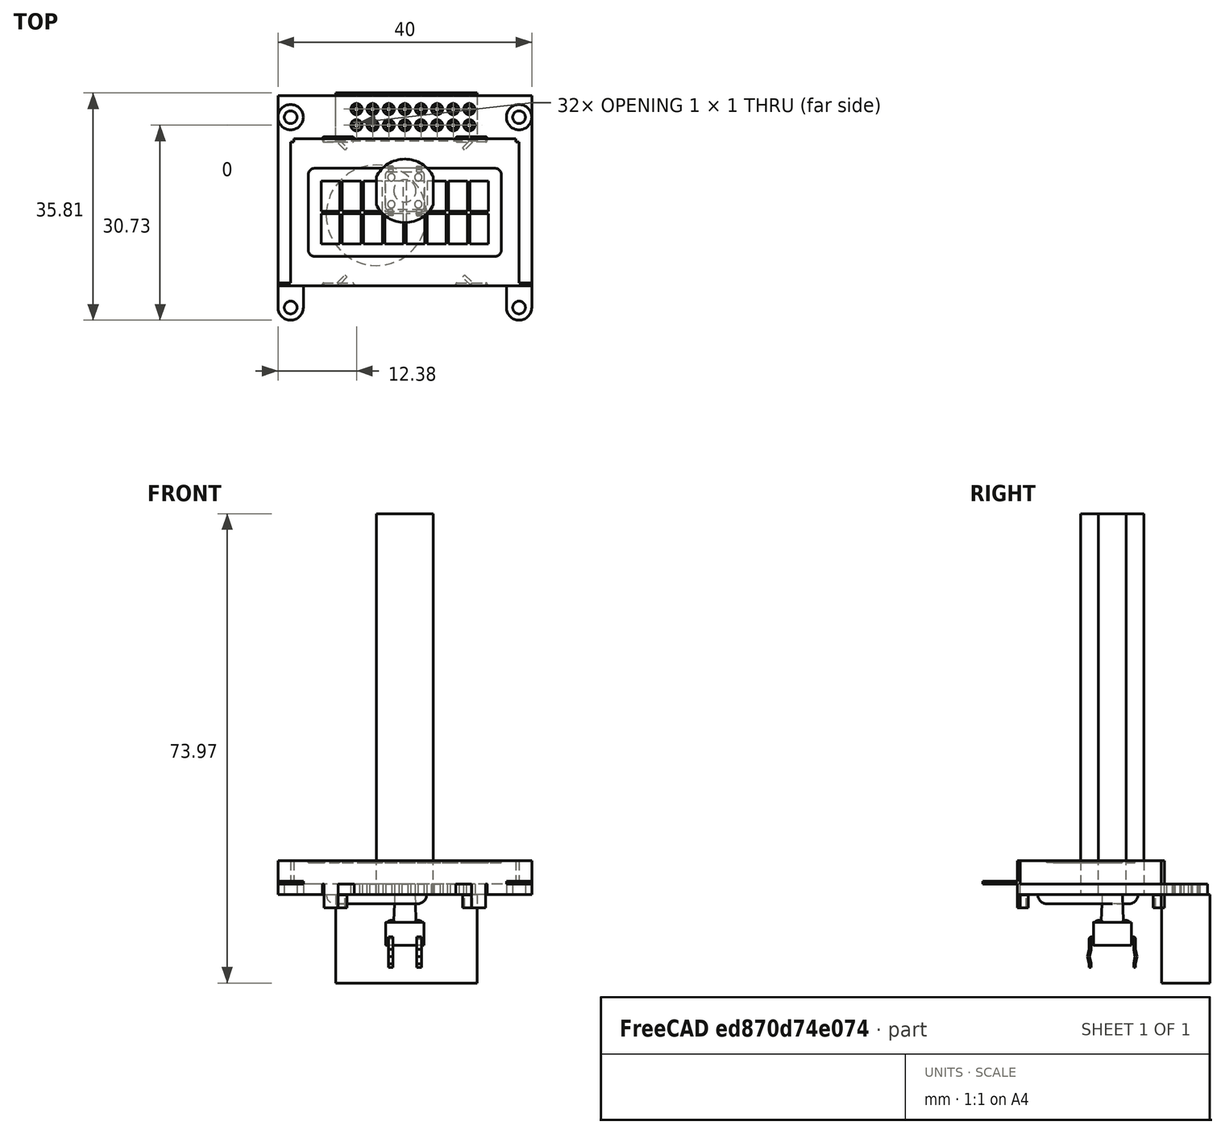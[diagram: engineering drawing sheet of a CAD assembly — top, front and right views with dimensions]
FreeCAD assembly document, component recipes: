
FREECAD ASSEMBLY — COMPONENT RECIPES ("WwvbClockComponents")

This assembly document has 6 components, labeled P0..P5 below (a component is one placed body or linked part). 4 of them carry a construction recipe — the FreeCAD feature program that regenerates the part from scratch, quoted from this document or its linked companion documents; the rest are supplied as boundary geometry only. No exploded tour is included for this assembly.
COMPONENT P0 — recipe-attached ("LCD panel001", modeled in this document).
Construction recipe (the document's own serialized feature program — sketch geometry with constraints, then the solid features built on it; lengths are millimeters unless a unit is written):

FEATURE [PartDesign::SubShapeBinder] Binder001
  BindCopyOnChange = 0
  BindMode = 0
  ClaimChildren = false
  Context = -> NHD_0208AZ_RN [Body.Binder001.]
  Fuse = false
  MakeFace = true
  OffsetFill = false
  OffsetIntersection = false
  OffsetJoinType = 0
  OffsetOpenResult = false
  PartialLoad = false
  Refine = true
  Relative = true
  Support = -> [Part__Feature018]
  _Version = 2
FEATURE [Sketcher::SketchObject] Sketch
  ArcFitTolerance = 1e-06
  AttachmentSupport = -> [Binder001]
  ExternalGeometry = -> [Binder001]
  FullyConstrained = true
  MakeInternals = false
  MapMode = 5
  Placement = pos=(0,0,0) rot=(1,0,0;3.14159rad)
  sketch-geometry (4):
    g0: LineSegment StartX=-10.922 StartY=-7.79 StartZ=0 EndX=-10.922 EndY=-15.41 EndZ=0
    g1: LineSegment StartX=-10.922 StartY=-15.41 StartZ=0 EndX=11.422 EndY=-15.41 EndZ=0
    g2: LineSegment StartX=11.422 StartY=-15.41 StartZ=0 EndX=11.422 EndY=-7.79 EndZ=0
    g3: LineSegment StartX=11.422 StartY=-7.79 StartZ=0 EndX=-10.922 EndY=-7.79 EndZ=0
  constraints (12):
    c: Coincident(g0,g1)
    c: Coincident(g1,g2)
    c: Coincident(g2,g3)
    c: Coincident(g3,g0)
    c: Vertical(g0)
    c: Vertical(g2)
    c: Horizontal(g1)
    c: Horizontal(g3)
    c: DistanceX(g0,g-4) = 3.302
    c: DistanceX(g-3,g2) = 3.302
    c: DistanceY(g0,g-4) = 2.54
    c: DistanceY(g-3,g2) = 2.54
FEATURE [PartDesign::Pad] Pad
  Direction = (0,0,-1)
  Length = 13.97
  Length2 = 10
  Profile = -> Sketch
  ReferenceAxis = -> Sketch [N_Axis]
  Refine = true
  Suppressed = false
  Type = 0
FEATURE [PartDesign::Body] Body
  AllowCompound = false
  Group = -> [Binder001,Sketch,Pad]
  Origin = -> Origin019
  Tip = -> Pad
COMPONENT P1 — recipe-attached ("LED", a linked part whose construction recipe lives in a companion FreeCAD document of the same project; that document's serialized recipe follows).
Construction recipe (the companion document, serialized — sketch geometry with constraints, then the solid features built on it; lengths are millimeters unless a unit is written):

FCSTD DOCUMENT  (FreeCAD 1.0R39109 (Git))
Label: ClockRaytrace
License: All rights reserved
LicenseURL: https://en.wikipedia.org/wiki/All_rights_reserved
objects: Part::FeaturePython×11, Sketcher::SketchObject×5, PartDesign::Body×4, PartDesign::Pad×4, App::Link×2, App::DocumentObjectGroup×2, PartDesign::Revolution×1, PartDesign::ShapeBinder×1, Spreadsheet::Sheet×1, App::Part×1
note: 41 computed .brp shape members not serialized (recipe doc carries the construction recipe); baked Part::Feature solids carry a one-line shape summary decoded from their .brp

FEATURE [Sketcher::SketchObject] Sketch001
  ArcFitTolerance = 1e-06
  AttachmentSupport = -> [XZ_Plane003]
  FullyConstrained = true
  MakeInternals = false
  MapMode = 5
  Placement = pos=(0,0,0) rot=(1,0,0;1.5708rad)
  sketch-geometry (7):
    g0: LineSegment StartX=0 StartY=3.99545 StartZ=0 EndX=0 EndY=-3.99545 EndZ=0
    g1: LineSegment [constr] StartX=0 StartY=0 StartZ=0 EndX=19 EndY=0 EndZ=0
    g2: LineSegment StartX=19 StartY=0.4 StartZ=0 EndX=19 EndY=-0.4 EndZ=0
    g3: Circle [constr] CenterX=0 CenterY=-48.0045 CenterZ=0 NormalX=0 NormalY=0 NormalZ=1 AngleXU=0 Radius=52
    g4: ArcOfCircle CenterX=1.31e-14 CenterY=-48.0045 CenterZ=0 NormalX=0 NormalY=0 NormalZ=1 AngleXU=0 Radius=52 StartAngle=1.19675 EndAngle=1.5708
    g5: Circle [constr] CenterX=0 CenterY=48.0045 CenterZ=0 NormalX=0 NormalY=0 NormalZ=1 AngleXU=0 Radius=52
    g6: ArcOfCircle CenterX=4.1e-15 CenterY=48.0045 CenterZ=0 NormalX=0 NormalY=0 NormalZ=1 AngleXU=0 Radius=52 StartAngle=4.71239 EndAngle=5.08643
  constraints (21):
    c: Vertical(g0)
    c: Symmetric(g0,g0,g-1)
    c: Coincident(g1,g-1)
    c: PointOnObject(g1,g-1)
    c: DistanceX(g1,g1) = 19
    c: Vertical(g2)
    c: Symmetric(g2,g2,g1)
    c: Radius(g3) = 52
    c: Vertical(g3,g0)
    c: PointOnObject(g2,g3)
    c: PointOnObject(g0,g3)
    c: Coincident(g4,g0)
    c: Coincident(g4,g2)
    c: Vertical(g5,g0)
    c: Equal(g5,g3)
    c: PointOnObject(g2,g5)
    c: Coincident(g6,g2)
    c: Coincident(g6,g0)
    c: Equal(g4,g3)
    c: Equal(g5,g6)
    c: DistanceY(g2,g2) = 0.8
FEATURE [PartDesign::Revolution] Revolution001
  Angle = 360
  Angle2 = 60
  Axis = (0,2e-16,1)
  Base = (0,0,0)
  Placement = pos=(0,0,0) rot=(1,0,0;1.5708rad)
  Profile = -> Sketch001
  ReferenceAxis = -> Sketch001 [V_Axis]
  Refine = true
  Reversed = true
  Suppressed = false
  Type = 0
FEATURE [PartDesign::Body] Body001  label="38mm50FLLens"
  AllowCompound = false
  Group = -> [Sketch001,Revolution001]
  Origin = -> Origin003
  Tip = -> Revolution001
FEATURE [Part::FeaturePython] Beam  # WARN: FeaturePython — macro-defined, semantics opaque (R4)
  BeamDistance = 0.1
  BeamNrColumns = 10
  BeamNrRows = 10
  ConeAngle = 90
  HideFirstPart = false
  MaxNrReflections = 200
  MaxRayLength = 1000000
  Order = 0
  Placement = pos=(1.855,-7.73,0) rot=(-1,0,0;0.05236rad)
  Power = true
  Spherical = true
  Wavelength = 580
  expr: .Placement.Base.x = Spreadsheet.Base_LED_Height / 2 + Spreadsheet.Base_LED_X_offset
  expr: .Placement.Base.y = -Spreadsheet.Base_LED_Width / 2
  expr: BeamNrColumns = Spreadsheet.Base_Source_Columns
  expr: BeamNrRows = Spreadsheet.Base_Source_Rows
  expr: ConeAngle = Spreadsheet.Base_SourceConeAngle
FEATURE [Part::FeaturePython] Beam001  # WARN: FeaturePython — macro-defined, semantics opaque (R4)
  BeamDistance = 0.1
  BeamNrColumns = 10
  BeamNrRows = 10
  ConeAngle = 90
  HideFirstPart = false
  MaxNrReflections = 200
  MaxRayLength = 1000000
  Order = 0
  Placement = pos=(-1.855,0,0) rot=(0,1,0;0rad)
  Power = true
  Spherical = true
  Wavelength = 580
  expr: .Placement.Base.x = -Spreadsheet.Base_LED_Height / 2 + Spreadsheet.Base_LED_X_offset
  expr: BeamNrColumns = Spreadsheet.Base_Source_Columns
  expr: BeamNrRows = Spreadsheet.Base_Source_Rows
  expr: ConeAngle = Spreadsheet.Base_SourceConeAngle
FEATURE [Part::FeaturePython] Beam002  # WARN: FeaturePython — macro-defined, semantics opaque (R4)
  BeamDistance = 1
  BeamNrColumns = 40
  BeamNrRows = 1
  ConeAngle = 360
  HideFirstPart = false
  MaxNrReflections = 200
  MaxRayLength = 1000000
  Order = 0
  Placement = pos=(20,0,0) rot=(0.57735,-0.57735,0.57735;2.0944rad)
  Power = true
  Spherical = false
  Wavelength = 580
FEATURE [Part::FeaturePython] Beam003  # WARN: FeaturePython — macro-defined, semantics opaque (R4)
  BeamDistance = 0.1
  BeamNrColumns = 10
  BeamNrRows = 10
  ConeAngle = 90
  HideFirstPart = false
  MaxNrReflections = 200
  MaxRayLength = 1000000
  Order = 0
  Placement = pos=(1.855,7.73,0) rot=(1,0,0;0.069813rad)
  Power = true
  Spherical = true
  Wavelength = 580
  expr: .Placement.Base.x = Spreadsheet.Base_LED_Height / 2 + Spreadsheet.Base_LED_X_offset
  expr: .Placement.Base.y = Spreadsheet.Base_LED_Width / 2
  expr: BeamNrColumns = Spreadsheet.Base_Source_Columns
  expr: BeamNrRows = Spreadsheet.Base_Source_Rows
  expr: ConeAngle = Spreadsheet.Base_SourceConeAngle
FEATURE [PartDesign::ShapeBinder] CopyPad004
  TraceSupport = false
FEATURE [Sketcher::SketchObject] Sketch
  ArcFitTolerance = 1e-06
  AttachmentSupport = -> [CopyPad004]
  FullyConstrained = true
  MakeInternals = false
  MapMode = 5
  Placement = pos=(0,0,0) rot=(1,0,0;3.14159rad)
  sketch-geometry (5):
    g0: LineSegment StartX=8.89 StartY=-5.08 StartZ=0 EndX=8.89 EndY=5.08 EndZ=0
    g1: LineSegment StartX=8.89 StartY=5.08 StartZ=0 EndX=-8.89 EndY=5.08 EndZ=0
    g2: LineSegment StartX=-8.89 StartY=5.08 StartZ=0 EndX=-8.89 EndY=-5.08 EndZ=0
    g3: LineSegment StartX=-8.89 StartY=-5.08 StartZ=0 EndX=8.89 EndY=-5.08 EndZ=0
    g4: GeomPoint [constr] X=0 Y=0 Z=0
  constraints (12):
    c: Coincident(g0,g1)
    c: Coincident(g1,g2)
    c: Coincident(g2,g3)
    c: Coincident(g3,g0)
    c: Vertical(g0)
    c: Vertical(g2)
    c: Horizontal(g1)
    c: Horizontal(g3)
    c: Symmetric(g2,g0,g4)
    c: Coincident(g4,g-1)
    c: DistanceY(g0,g0) = 10.16
    c: DistanceX(g1,g1) = 17.78
FEATURE [PartDesign::Pad] Pad
  Direction = (0,0,-1)
  Length = 5.08
  Length2 = 10
  Profile = -> Sketch
  ReferenceAxis = -> Sketch [N_Axis]
  Refine = true
  Reversed = true
  Suppressed = false
  Type = 0
FEATURE [Sketcher::SketchObject] Sketch011
  ArcFitTolerance = 1e-06
  AttachmentSupport = -> [XY_Plane019]
  FullyConstrained = false
  MakeInternals = false
  MapMode = 5
  sketch-geometry (3):
    g0: Circle CenterX=0 CenterY=0 CenterZ=0 NormalX=0 NormalY=0 NormalZ=1 AngleXU=0 Radius=20
    g1: Circle CenterX=0 CenterY=0 CenterZ=0 NormalX=0 NormalY=0 NormalZ=1 AngleXU=0 Radius=21.5748
    g2: LineSegment [constr] StartX=0.010426 StartY=20 StartZ=0 EndX=0.010426 EndY=21.5748 EndZ=0
  constraints (7):
    c: Coincident(g0,g-1)
    c: Coincident(g1,g0)
    c: Diameter(g0) = 40
    c: PointOnObject(g2,g0)
    c: PointOnObject(g2,g1)
    c: Vertical(g2)
    c: DistanceY(g2,g2) = 1.5748
FEATURE [PartDesign::Pad] Pad006
  Direction = (0,0,1)
  Length = 48
  Length2 = 10
  Profile = -> Sketch011
  ReferenceAxis = -> Sketch011 [N_Axis]
  Refine = true
  Reversed = true
  Suppressed = false
  Type = 0
  expr: Length = Spreadsheet.Base_LensToLED - 3 mm
FEATURE [PartDesign::Body] Body010  label="baffle"
  AllowCompound = false
  Group = -> [Sketch011,Pad006]
  Origin = -> Origin019
  Placement = pos=(-7.46,0,48) rot=(0,-1,0;0.314159rad)
  Tip = -> Pad006
  expr: .Placement.Base.x = 2.54 mm - Spreadsheet.Base_Lens_X_offset
  expr: .Placement.Base.z = Spreadsheet.Base_LensToLED - 3 mm
FEATURE [Part::FeaturePython] Absorber001  # WARN: FeaturePython — macro-defined, semantics opaque (R4)
  Base = -> [Body010]
  OpticalType = 1
  Transparency = 0
  collectStatistics = false
FEATURE [Spreadsheet::Sheet] Spreadsheet
  Base_Ceiling_Target_Height = 101.6
  Base_Ceiling_Target_Width = 254
  Base_DeviceTilt = 0
  Base_LED_Height = 3.71
  Base_LED_Package_Height = 5.08
  Base_LED_Width = 15.46
  Base_LED_X_offset = 0
  Base_LED_Y_offset = 0
  Base_LED_yaw_angle = 90
  Base_LEDtoCeiling = 1397
  Base_LensToLED = 51
  Base_Lens_X_offset = 10
  Base_SourceConeAngle = 90
  Base_Source_Columns = 10
  Base_Source_Rows = 10
  Base_XOffset_LED_to_Ceiling = -248.158
FEATURE [Part::FeaturePython] Beam004  # WARN: FeaturePython — macro-defined, semantics opaque (R4)
  BeamDistance = 0.1
  BeamNrColumns = 10
  BeamNrRows = 10
  ConeAngle = 90
  HideFirstPart = false
  MaxNrReflections = 200
  MaxRayLength = 1000000
  Order = 0
  Placement = pos=(-1.855,-7.73,0) rot=(-1,0,0;0.05236rad)
  Power = true
  Spherical = true
  Wavelength = 580
  expr: .Placement.Base.x = -Spreadsheet.Base_LED_Height / 2 + Spreadsheet.Base_LED_X_offset
  expr: .Placement.Base.y = -Spreadsheet.Base_LED_Width / 2
  expr: BeamNrColumns = Spreadsheet.Base_Source_Columns
  expr: BeamNrRows = Spreadsheet.Base_Source_Rows
  expr: ConeAngle = Spreadsheet.Base_SourceConeAngle
FEATURE [Part::FeaturePython] Beam005  # WARN: FeaturePython — macro-defined, semantics opaque (R4)
  BeamDistance = 0.1
  BeamNrColumns = 10
  BeamNrRows = 10
  ConeAngle = 90
  HideFirstPart = false
  MaxNrReflections = 200
  MaxRayLength = 1000000
  Order = 0
  Placement = pos=(1.855,0,0) rot=(-1,0,0;0.05236rad)
  Power = true
  Spherical = true
  Wavelength = 580
  expr: .Placement.Base.x = Spreadsheet.Base_LED_Height / 2 + <<Spreadsheet>>.Base_LED_X_offset
  expr: .Placement.Base.y = 0 in
  expr: BeamNrColumns = Spreadsheet.Base_Source_Columns
  expr: BeamNrRows = Spreadsheet.Base_Source_Rows
  expr: ConeAngle = Spreadsheet.Base_SourceConeAngle
FEATURE [Part::FeaturePython] Beam006  # WARN: FeaturePython — macro-defined, semantics opaque (R4)
  BeamDistance = 0.1
  BeamNrColumns = 10
  BeamNrRows = 10
  ConeAngle = 90
  HideFirstPart = false
  MaxNrReflections = 200
  MaxRayLength = 1000000
  Order = 0
  Placement = pos=(-1.855,7.73,0) rot=(1,0,0;0.069813rad)
  Power = true
  Spherical = true
  Wavelength = 580
  expr: .Placement.Base.x = -Spreadsheet.Base_LED_Height / 2 + Spreadsheet.Base_LED_X_offset
  expr: .Placement.Base.y = Spreadsheet.Base_LED_Width / 2
  expr: BeamNrColumns = Spreadsheet.Base_Source_Columns
  expr: BeamNrRows = Spreadsheet.Base_Source_Rows
  expr: ConeAngle = Spreadsheet.Base_SourceConeAngle
FEATURE [Sketcher::SketchObject] Sketch012
  ArcFitTolerance = 1e-06
  AttachmentSupport = -> [XZ_Plane022]
  FullyConstrained = true
  MakeInternals = false
  MapMode = 5
  Placement = pos=(0,0,0) rot=(0,0.707107,0.707107;3.14159rad)
  sketch-geometry (6):
    g0: LineSegment StartX=-76.2 StartY=0 StartZ=0 EndX=-76.2 EndY=1390.42 EndZ=0
    g1: LineSegment StartX=-76.2 StartY=1390.42 StartZ=0 EndX=1751.03 EndY=1390.42 EndZ=0
    g2: LineSegment StartX=1751.03 StartY=1390.42 StartZ=0 EndX=1751.03 EndY=1391.99 EndZ=0
    g3: LineSegment StartX=1751.03 StartY=1391.99 StartZ=0 EndX=-77.7748 EndY=1391.99 EndZ=0
    g4: LineSegment StartX=-77.7748 StartY=1391.99 StartZ=0 EndX=-77.7748 EndY=0 EndZ=0
    g5: LineSegment StartX=-77.7748 StartY=0 StartZ=0 EndX=-76.2 EndY=0 EndZ=0
  constraints (18):
    c: Vertical(g0)
    c: Horizontal(g1)
    c: Coincident(g2,g1)
    c: Vertical(g2)
    c: Horizontal(g3)
    c: PointOnObject(g4,g-1)
    c: Vertical(g4)
    c: Coincident(g5,g0)
    c: DistanceY(g2,g2) = 1.5748
    c: Equal(g5,g2)
    c: Coincident(g3,g2)
    c: Coincident(g3,g4)
    c: Coincident(g1,g0)
    c: Coincident(g5,g4)
    c: DistanceX(g0,g-1) = 76.2
    c: DistanceY(g4,g4) = 1391.99
    c: DistanceX(g3,g3) = 1828.8
    c: Horizontal(g0,g-1)
FEATURE [PartDesign::Pad] Pad007
  Direction = (0,1,-2e-16)
  Length = 1524
  Length2 = 10
  Midplane = true
  Placement = pos=(0,0,0) rot=(1,0,0;1.5708rad)
  Profile = -> Sketch012
  ReferenceAxis = -> Sketch012 [N_Axis]
  Refine = true
  Suppressed = false
  Type = 0
FEATURE [PartDesign::Body] Body011  label="Wall and Ceiling"
  AllowCompound = false
  Group = -> [Sketch012,Pad007]
  Origin = -> Origin020
  Tip = -> Pad007
  expr: .Placement.Rotation.Pitch = Spreadsheet.Base_DeviceTilt
FEATURE [Part::FeaturePython] Absorber  # WARN: FeaturePython — macro-defined, semantics opaque (R4)
  Base = -> [Body011]
  OpticalType = 1
  Transparency = 0
  collectStatistics = false
FEATURE [Sketcher::SketchObject] Sketch013
  ArcFitTolerance = 1e-06
  AttachmentSupport = -> [CopyPad004]
  FullyConstrained = true
  MakeInternals = false
  MapMode = 5
  Placement = pos=(0,0,0) rot=(1,0,0;3.14159rad)
  sketch-geometry (9):
    g0: LineSegment [constr] StartX=6.35 StartY=-3.81 StartZ=0 EndX=6.35 EndY=3.81 EndZ=0
    g1: LineSegment [constr] StartX=6.35 StartY=3.81 StartZ=0 EndX=-6.35 EndY=3.81 EndZ=0
    g2: LineSegment [constr] StartX=-6.35 StartY=3.81 StartZ=0 EndX=-6.35 EndY=-3.81 EndZ=0
    g3: LineSegment [constr] StartX=-6.35 StartY=-3.81 StartZ=0 EndX=6.35 EndY=-3.81 EndZ=0
    g4: GeomPoint [constr] X=0 Y=0 Z=0
    g5: Circle CenterX=-6.35 CenterY=-3.81 CenterZ=0 NormalX=0 NormalY=0 NormalZ=1 AngleXU=0 Radius=0.3175
    g6: Circle CenterX=6.35 CenterY=-3.81 CenterZ=0 NormalX=0 NormalY=0 NormalZ=1 AngleXU=0 Radius=0.3175
    g7: Circle CenterX=6.35 CenterY=3.81 CenterZ=0 NormalX=0 NormalY=0 NormalZ=1 AngleXU=0 Radius=0.3175
    g8: Circle CenterX=-6.35 CenterY=3.81 CenterZ=0 NormalX=0 NormalY=0 NormalZ=1 AngleXU=0 Radius=0.3175
  constraints (20):
    c: Coincident(g0,g1)
    c: Coincident(g1,g2)
    c: Coincident(g2,g3)
    c: Coincident(g3,g0)
    c: Vertical(g0)
    c: Vertical(g2)
    c: Horizontal(g1)
    c: Horizontal(g3)
    c: Symmetric(g2,g0,g4)
    c: Coincident(g4,g-1)
    c: DistanceX(g1,g1) = 12.7
    c: DistanceY(g2,g2) = 7.62
    c: Coincident(g5,g2)
    c: Coincident(g6,g0)
    c: Coincident(g7,g0)
    c: Coincident(g8,g1)
    c: Equal(g5,g8)
    c: Equal(g7,g8)
    c: Equal(g6,g8)
    c: Diameter(g8) = 0.635
FEATURE [PartDesign::Pad] Pad008
  BaseFeature = -> Pad
  Direction = (0,0,-1)
  Length = 4.318
  Length2 = 10
  Profile = -> Sketch013
  ReferenceAxis = -> Sketch013 [N_Axis]
  Refine = true
  Suppressed = false
  Type = 0
FEATURE [PartDesign::Body] Body
  AllowCompound = false
  Group = -> [CopyPad004,Sketch,Pad,Sketch013,Pad008]
  Origin = -> Origin
  Tip = -> Pad008
FEATURE [App::Part] Part006  label="LED"
  Group = -> [Body]
  Origin = -> Origin013
  Placement = pos=(0,0,-5.08) rot=(0,0,1;1.5708rad)
  expr: .Placement.Base.x = Spreadsheet.Base_LED_X_offset
  expr: .Placement.Base.z = -Spreadsheet.Base_LED_Package_Height
  expr: .Placement.Rotation.Yaw = Spreadsheet.Base_LED_yaw_angle
FEATURE [App::Link] Link  label="LED001"
  LinkPlacement = pos=(10.16,0,-5.08) rot=(0,0,1;1.5708rad)
  LinkedObject = -> Part006
  Placement = pos=(10.16,0,-5.08) rot=(0,0,1;1.5708rad)
  expr: .Placement.Base.x = Spreadsheet.Base_LED_X_offset + 400 thou
FEATURE [Part::FeaturePython] Beam007  # WARN: FeaturePython — macro-defined, semantics opaque (R4)
  BeamDistance = 0.1
  BeamNrColumns = 10
  BeamNrRows = 10
  ConeAngle = 90
  HideFirstPart = false
  MaxNrReflections = 200
  MaxRayLength = 1000000
  Order = 0
  Placement = pos=(12.015,-7.62,0) rot=(0,0,1;0rad)
  Power = true
  Spherical = true
  Wavelength = 580
  expr: .Placement.Base.x = Spreadsheet.Base_LED_Height / 2 + Spreadsheet.Base_LED_X_offset + 400 thou
  expr: BeamNrColumns = Spreadsheet.Base_Source_Columns
  expr: BeamNrRows = Spreadsheet.Base_Source_Rows
  expr: ConeAngle = Spreadsheet.Base_SourceConeAngle
FEATURE [App::DocumentObjectGroup] Group001  label="LED2"
  Group = -> [Beam007]
FEATURE [App::DocumentObjectGroup] Group  label="sources"
  Group = -> [Beam,Beam001,Beam003,Beam004,Beam005,Beam006,Group001]
FEATURE [App::Link] Link001  label="38mm50FLLens001"
  LinkPlacement = pos=(-10,0,51) rot=(0,0,1;0rad)
  LinkedObject = -> Body001
  Placement = pos=(-10,0,51) rot=(0,0,1;0rad)
  expr: .Placement.Base.x = -Spreadsheet.Base_Lens_X_offset
  expr: .Placement.Base.z = Spreadsheet.Base_LensToLED
FEATURE [Part::FeaturePython] Lens  # WARN: FeaturePython — macro-defined, semantics opaque (R4)
  Base = -> [Link001]
  Material = 3
  OpticalType = 0
  RefractionIndex = 1.45873
  Sellmeier = [0.696166,0.407943,0.897479,4679.15,13512.1,97934000]
  Transparency = 100
  collectStatistics = false
COMPONENT P2 — same part as P1; its construction recipe is shown at P1.
COMPONENT P3 — geometry summary ("Switch 003"; no construction recipe available for this part):
  bounding box: 11.5 x 7.8 x 6.0 mm
  tessellated surface: 17,072 triangles
  volume: 173 mm^3 (32% of its bounding box)
  symmetry: 2-fold rotationally symmetric about the z axis; mirror-symmetric across its x mid-plane, y mid-plane
COMPONENT P4 — geometry summary ("Switch 002"; no construction recipe available for this part):
  bounding box: 11.5 x 7.8 x 6.0 mm
  tessellated surface: 17,072 triangles
  volume: 173 mm^3 (32% of its bounding box)
  symmetry: 2-fold rotationally symmetric about the z axis; mirror-symmetric across its x mid-plane, y mid-plane
COMPONENT P5 — same part as P1; its construction recipe is shown at P1.
PROVENANCE & LICENSES
A FreeCAD (.FCStd) document from a public repository crawl; recipes are the document's own serialized feature recipes (and, for linked parts, companion documents' recipes).
License: mit.
